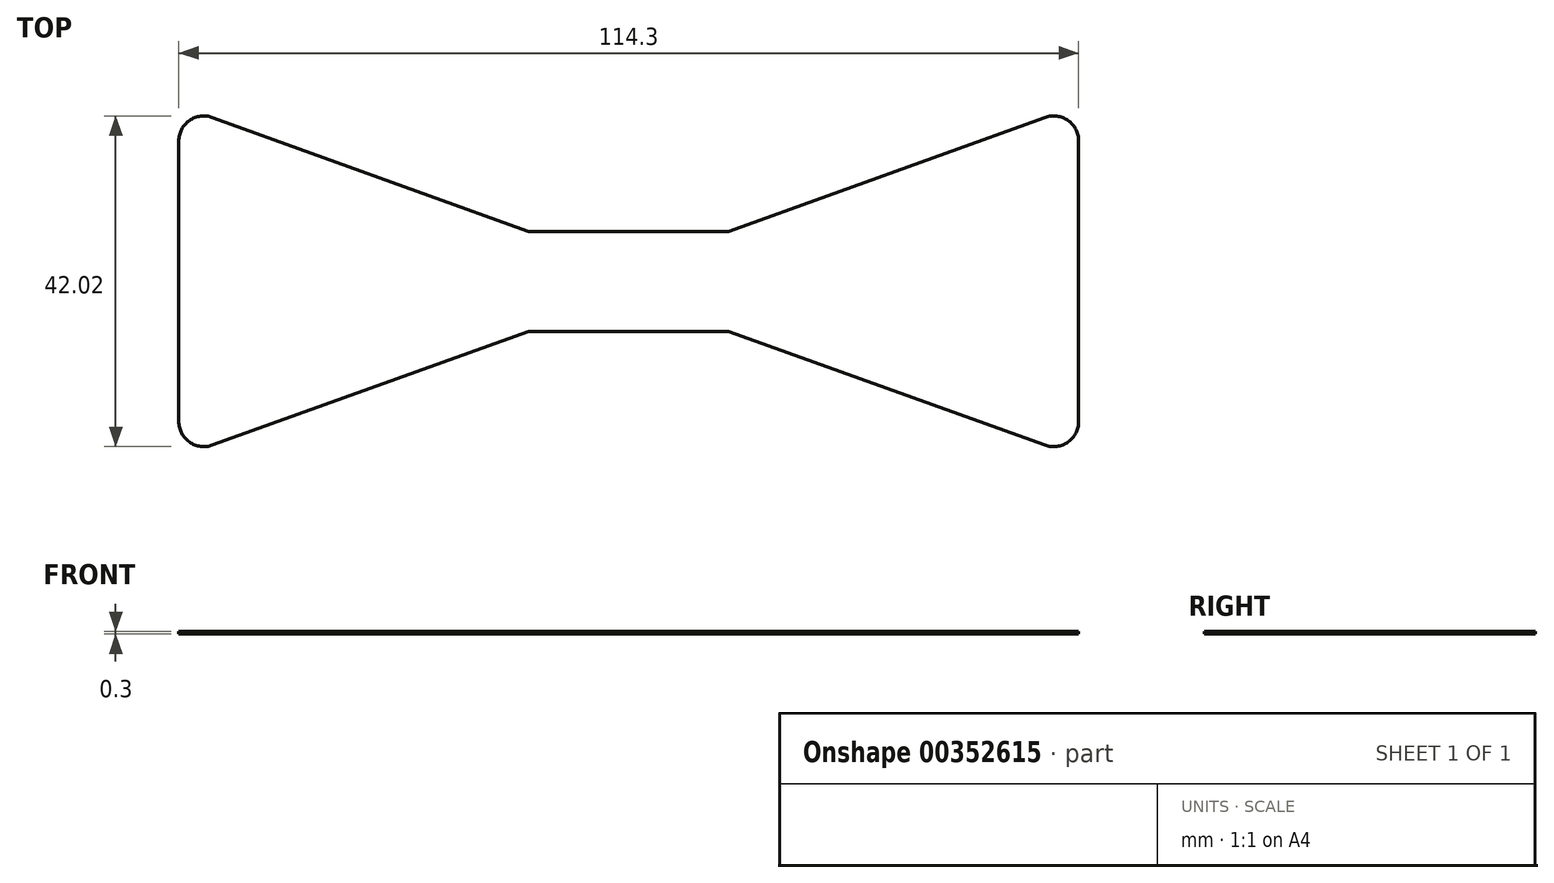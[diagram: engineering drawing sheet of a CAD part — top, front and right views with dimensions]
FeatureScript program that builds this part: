
annotation { "Feature Type Name" : "Feature", "Feature Type Description" : "" }
export const myFeature = defineFeature(function(context is Context, id is Id, definition is map)
    precondition{}
    {
        {
            var Q0;
            Q0=qCreatedBy(makeId("Top.planeOp"),FACE);
            var sketch = newSketch(context, id + "F0", { "sketchPlane" : qUnion([Q0])});
            skLineSegment(sketch, "E0", {"start": v(0, 0) * mm, "end": v(57.15, 0) * mm});
            skLineSegment(sketch, "E1", {"start": v(0, 0) * mm, "end": v(-57.15, 0) * mm});
            skLineSegment(sketch, "E2.bottom", {"start": v(12.7, -6.35) * mm, "end": v(-12.7, -6.35) * mm});
            skLineSegment(sketch, "E2.top", {"start": v(12.7, 6.35) * mm, "end": v(-12.7, 6.35) * mm});
            skLineSegment(sketch, "E2.left", {"start": v(12.7, -6.35) * mm, "end": v(12.7, 6.35) * mm});
            skLineSegment(sketch, "E2.right", {"start": v(-12.7, -6.35) * mm, "end": v(-12.7, 6.35) * mm});
            skPoint(sketch, "E2.middle", {"position": v(0, 0) * mm});
            skLineSegment(sketch, "E3", {"start": v(-57.15, 0) * mm, "end": v(-57.15, 17.83) * mm});
            skLineSegment(sketch, "E4", {"start": v(-57.15, 0) * mm, "end": v(-57.15, -17.83) * mm});
            skLineSegment(sketch, "E5", {"start": v(57.15, 0) * mm, "end": v(57.15, 17.83) * mm});
            skLineSegment(sketch, "E6", {"start": v(57.15, 0) * mm, "end": v(57.15, -17.83) * mm});
            skLineSegment(sketch, "E7", {"start": v(-52.9, 20.82) * mm, "end": v(-12.7, 6.35) * mm});
            skLineSegment(sketch, "E8", {"start": v(12.7, 6.35) * mm, "end": v(52.9, 20.82) * mm});
            skLineSegment(sketch, "E9", {"start": v(12.7, -6.35) * mm, "end": v(52.9, -20.82) * mm});
            skLineSegment(sketch, "E10", {"start": v(-12.7, -6.35) * mm, "end": v(-52.9, -20.82) * mm});
            skPoint(sketch, "E11.visualSharp", {"position": v(-57.15, 22.35) * mm});
            skArc(sketch, "E11.filletArc", {"start": v(-52.9, 20.82) * mm, "mid": v(-55.8, 20.43) * mm, "end": v(-57.15, 17.83) * mm});
            skPoint(sketch, "E12.visualSharp", {"position": v(-57.15, -22.35) * mm});
            skArc(sketch, "E12.filletArc", {"start": v(-57.15, -17.83) * mm, "mid": v(-55.8, -20.43) * mm, "end": v(-52.9, -20.82) * mm});
            skPoint(sketch, "E13.visualSharp", {"position": v(57.15, -22.35) * mm});
            skArc(sketch, "E13.filletArc", {"start": v(52.9, -20.82) * mm, "mid": v(55.8, -20.43) * mm, "end": v(57.15, -17.83) * mm});
            skPoint(sketch, "E14.visualSharp", {"position": v(57.15, 22.35) * mm});
            skArc(sketch, "E14.filletArc", {"start": v(57.15, 17.83) * mm, "mid": v(55.8, 20.43) * mm, "end": v(52.9, 20.82) * mm});
            skSolve(sketch);
        }
        {
            var Q0;
            Q0 = qSketchRegion(id + "F0", true);
            extrude(context, id + "F1", {"entities" : qUnion([Q0]), "depth" : 0.3 * mm, "offsetDistance" : 25.4 * mm});
        }
    });
